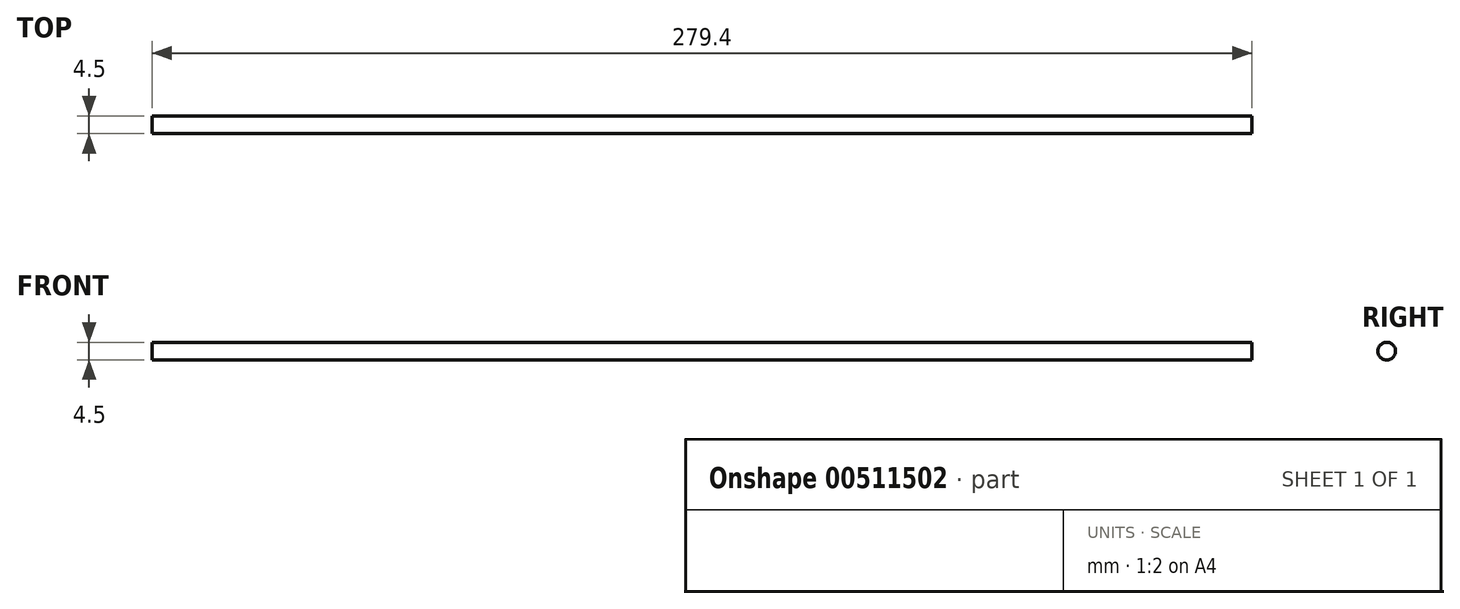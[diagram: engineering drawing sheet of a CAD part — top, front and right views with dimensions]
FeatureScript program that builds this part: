
annotation { "Feature Type Name" : "Feature", "Feature Type Description" : "" }
export const myFeature = defineFeature(function(context is Context, id is Id, definition is map)
    precondition{}
    {
        {
            var Q0;
            Q0=qCreatedBy(makeId("Right.planeOp"),FACE);
            var sketch = newSketch(context, id + "F0", { "sketchPlane" : qUnion([Q0])});
            skCircle(sketch, "E0", {"center": v(0, 0) * mm, "radius": 2.25 * mm});
            skSolve(sketch);
        }
        {
            var Q0;
            Q0 = qSketchRegion(id + "F0", true);
            extrude(context, id + "F1", {"entities" : qUnion([Q0]), "depth" : 279.4 * mm});
        }
    });
